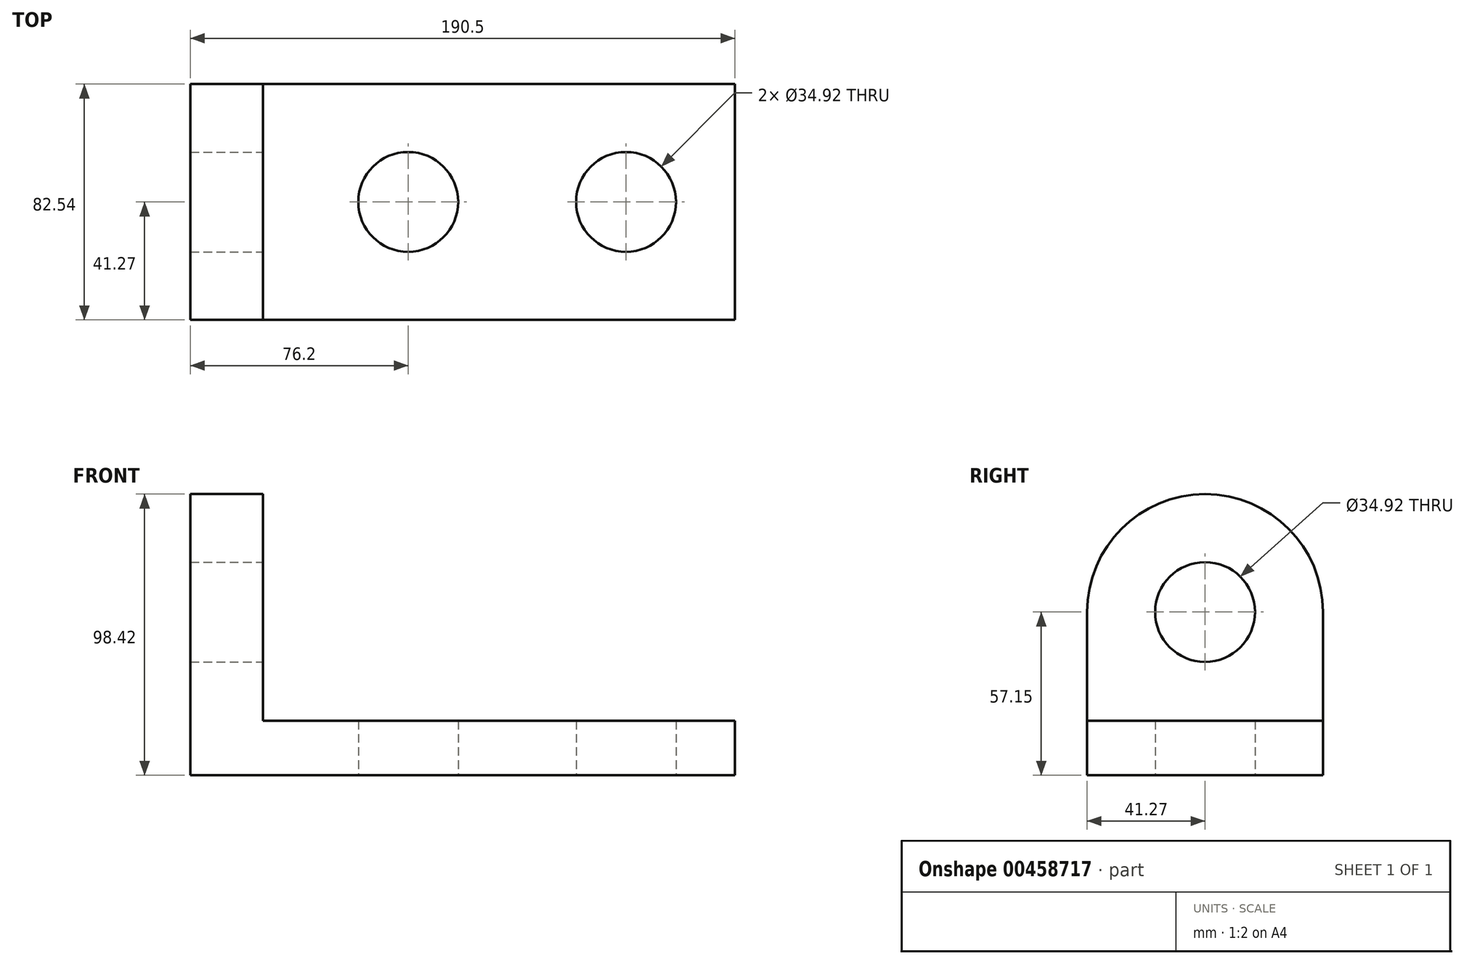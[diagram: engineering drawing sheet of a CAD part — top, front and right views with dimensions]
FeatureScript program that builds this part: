
annotation { "Feature Type Name" : "Feature", "Feature Type Description" : "" }
export const myFeature = defineFeature(function(context is Context, id is Id, definition is map)
    precondition{}
    {
        {
            var Q0;
            Q0=qCreatedBy(makeId("Top.planeOp"),FACE);
            var sketch = newSketch(context, id + "F0", { "sketchPlane" : qUnion([Q0])});
            skLineSegment(sketch, "E0.bottom", {"start": v(95.25, 41.28) * mm, "end": v(-95.25, 41.27) * mm});
            skLineSegment(sketch, "E0.top", {"start": v(95.25, -41.27) * mm, "end": v(-95.25, -41.28) * mm});
            skLineSegment(sketch, "E0.left", {"start": v(95.25, 41.28) * mm, "end": v(95.25, -41.27) * mm});
            skLineSegment(sketch, "E0.right", {"start": v(-95.25, 41.27) * mm, "end": v(-95.25, -41.28) * mm});
            skPoint(sketch, "E0.middle", {"position": v(0, 0) * mm});
            skLineSegment(sketch, "E1", {"start": v(-69.85, 41.27) * mm, "end": v(-69.85, -41.28) * mm});
            skCircle(sketch, "E2", {"center": v(-19.05, 0) * mm, "radius": 17.46 * mm});
            skCircle(sketch, "E3", {"center": v(57.15, 0) * mm, "radius": 17.46 * mm});
            skSolve(sketch);
        }
        {
            var Q0;
            Q0 = qSketchRegion(id + "F0", true);
            extrude(context, id + "F1", {"entities" : qUnion([Q0]), "depth" : 19.05 * mm});
        }
        {
            var Q0;
            {var subQ0=sQuery(id+"F0.wireOp",EDGE,"E0.right");Q0=makeQuery(id+"F0.imprint","IMPRINT",FACE,{"disambiguationData":[TD([[makeQuery(id+"F0.imprint","IMPRINT",EDGE,{"derivedFrom":subQ0}),1.0]])]});}
            extrude(context, id + "F2", {"entities" : qUnion([Q0]), "operationType" : NewBodyOperationType.ADD, "depth" : 57.15 * mm});
        }
        {
            var Q0;
            Q0=makeQuery(id+"F2.opExtrude","SWEPT_FACE",FACE,{"disambiguationData":[OSD([sQuery(id+"F0.wireOp",EDGE,"E1")])]});
            var sketch = newSketch(context, id + "F3", { "sketchPlane" : qUnion([Q0])});
            skCircle(sketch, "E4", {"center": v(0, 57.15) * mm, "radius": 17.46 * mm});
            skArc(sketch, "E5", {"start": v(41.28, 57.15) * mm, "mid": v(0, 98.43) * mm, "end": v(-41.28, 57.15) * mm});
            skSolve(sketch);
        }
        {
            var Q0;
            {var subQ5=sQuery(id+"F3.wireOp",EDGE,"E5");Q0=makeQuery(id+"F3.imprint","IMPRINT",FACE,{"disambiguationData":[TD([[makeQuery(id+"F3.imprint","IMPRINT",EDGE,{"derivedFrom":subQ5}),1.0]])]});}
            extrude(context, id + "F4", {"entities" : qUnion([Q0]), "operationType" : NewBodyOperationType.ADD, "oppositeDirection" : true, "depth" : 25.4 * mm});
        }
        {
            var Q0;
            Q0 = qSketchRegion(id + "F3", true);
            extrude(context, id + "F5", {"entities" : qUnion([Q0]), "operationType" : NewBodyOperationType.REMOVE, "oppositeDirection" : true, "depth" : 25.4 * mm});
        }
    });
